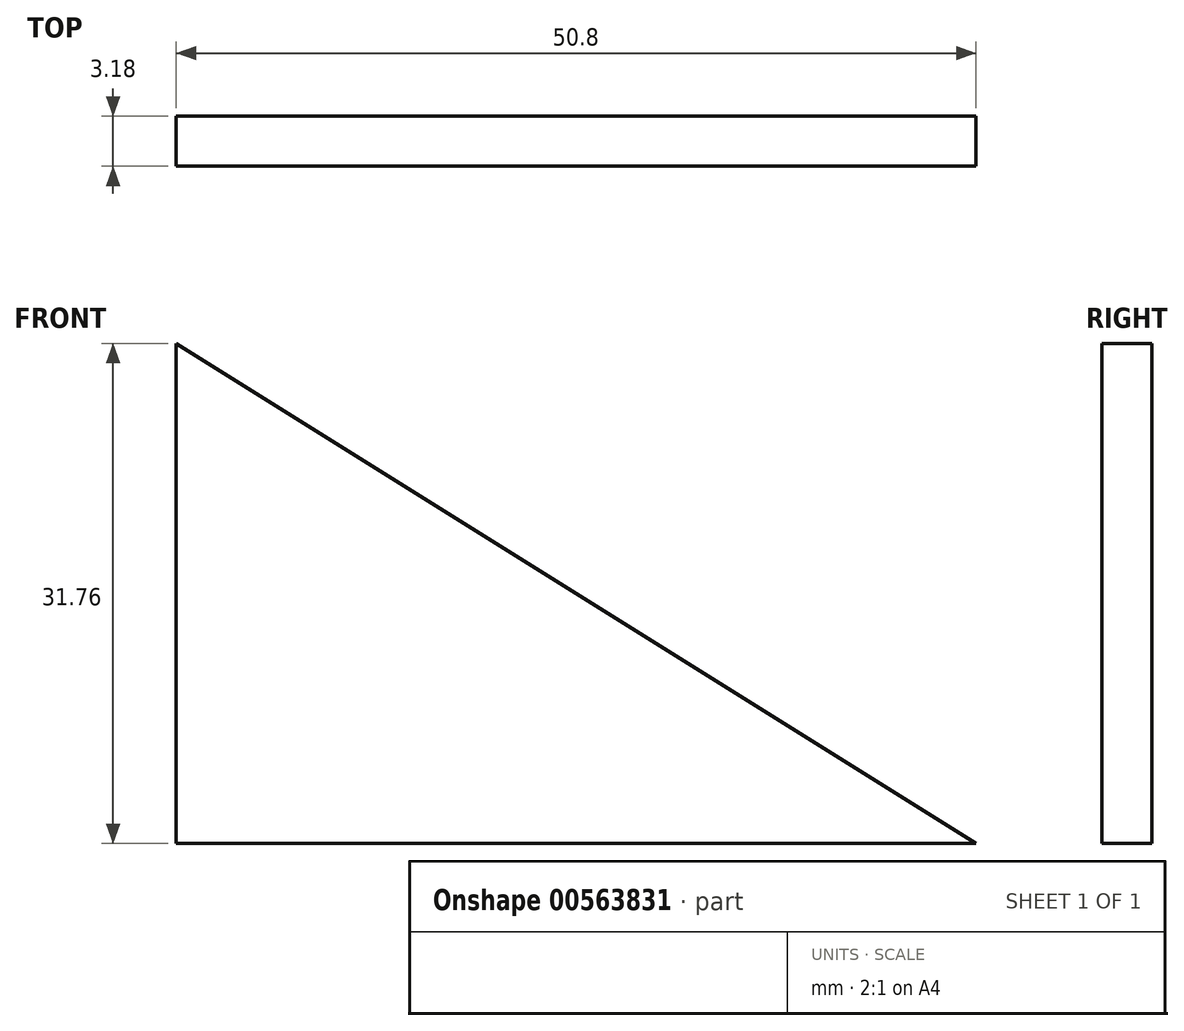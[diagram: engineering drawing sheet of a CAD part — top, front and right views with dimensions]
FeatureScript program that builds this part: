
annotation { "Feature Type Name" : "Feature", "Feature Type Description" : "" }
export const myFeature = defineFeature(function(context is Context, id is Id, definition is map)
    precondition{}
    {
        {
            var Q0;
            Q0=qCreatedBy(makeId("Front.planeOp"),FACE);
            var sketch = newSketch(context, id + "F0", { "sketchPlane" : qUnion([Q0])});
            skLineSegment(sketch, "E0.bottom", {"start": v(-25.4, 15.88) * mm, "end": v(25.4, 15.88) * mm});
            skLineSegment(sketch, "E0.top", {"start": v(-25.4, -15.88) * mm, "end": v(25.4, -15.88) * mm});
            skLineSegment(sketch, "E0.left", {"start": v(-25.4, 15.88) * mm, "end": v(-25.4, -15.88) * mm});
            skLineSegment(sketch, "E0.right", {"start": v(25.4, 15.88) * mm, "end": v(25.4, -15.88) * mm});
            skPoint(sketch, "E0.middle", {"position": v(0, 0) * mm});
            skLineSegment(sketch, "E1", {"start": v(-25.4, 15.88) * mm, "end": v(25.4, -15.88) * mm});
            skSolve(sketch);
        }
        {
            var Q0;
            Q0=makeQuery(id+"F0.imprint","IMPRINT",FACE,{"disambiguationData":[TD([[makeQuery(id+"F0.imprint","IMPRINT",EDGE,{"derivedFrom":sQuery(id+"F0.wireOp",EDGE,"E0.top")}),1.0]])]});
            extrude(context, id + "F1", {"entities" : qUnion([Q0]), "endBound" : BoundingType.SYMMETRIC, "depth" : 3.17 * mm, "offsetDistance" : 25.4 * mm});
        }
    });
